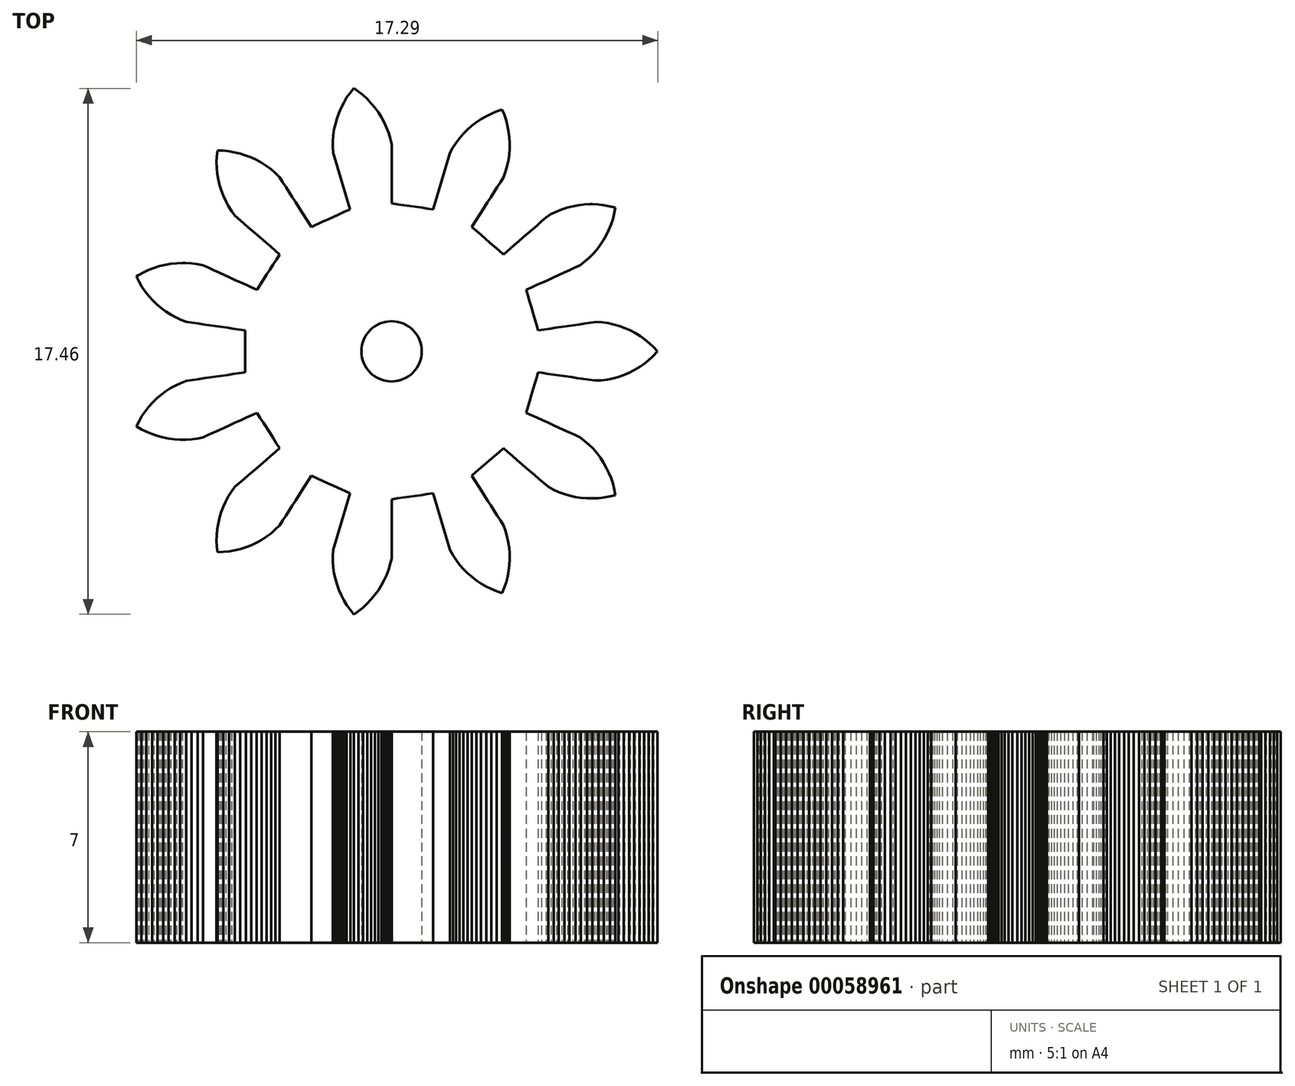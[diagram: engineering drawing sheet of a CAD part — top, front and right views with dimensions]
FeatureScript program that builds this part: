
annotation { "Feature Type Name" : "Feature", "Feature Type Description" : "" }
export const myFeature = defineFeature(function(context is Context, id is Id, definition is map)
    precondition{}
    {
        {
            var Q0;
            Q0=qCreatedBy(makeId("Top.planeOp"),FACE);
            var sketch = newSketch(context, id + "F0", { "sketchPlane" : qUnion([Q0])});
            skLineSegment(sketch, "E0", {"start": v(3.47, -0.7) * mm, "end": v(3.6, -0.72) * mm});
            skLineSegment(sketch, "E1", {"start": v(3.6, -0.72) * mm, "end": v(3.8, -0.75) * mm});
            skLineSegment(sketch, "E2", {"start": v(3.8, -0.75) * mm, "end": v(4, -0.77) * mm});
            skLineSegment(sketch, "E3", {"start": v(4, -0.77) * mm, "end": v(4.19, -0.8) * mm});
            skLineSegment(sketch, "E4", {"start": v(4.19, -0.8) * mm, "end": v(4.38, -0.83) * mm});
            skLineSegment(sketch, "E5", {"start": v(4.38, -0.83) * mm, "end": v(4.58, -0.86) * mm});
            skLineSegment(sketch, "E6", {"start": v(4.58, -0.86) * mm, "end": v(4.77, -0.89) * mm});
            skLineSegment(sketch, "E7", {"start": v(4.77, -0.89) * mm, "end": v(4.96, -0.91) * mm});
            skLineSegment(sketch, "E8", {"start": v(4.96, -0.91) * mm, "end": v(5.16, -0.94) * mm});
            skLineSegment(sketch, "E9", {"start": v(5.16, -0.94) * mm, "end": v(5.35, -0.97) * mm});
            skLineSegment(sketch, "E10", {"start": v(5.35, -0.97) * mm, "end": v(5.57, -0.97) * mm});
            skLineSegment(sketch, "E11", {"start": v(5.57, -0.97) * mm, "end": v(5.77, -0.94) * mm});
            skLineSegment(sketch, "E12", {"start": v(5.77, -0.94) * mm, "end": v(5.95, -0.9) * mm});
            skLineSegment(sketch, "E13", {"start": v(5.95, -0.9) * mm, "end": v(6.14, -0.85) * mm});
            skLineSegment(sketch, "E14", {"start": v(6.14, -0.85) * mm, "end": v(6.32, -0.79) * mm});
            skLineSegment(sketch, "E15", {"start": v(6.32, -0.79) * mm, "end": v(6.5, -0.7) * mm});
            skLineSegment(sketch, "E16", {"start": v(6.5, -0.7) * mm, "end": v(6.66, -0.62) * mm});
            skLineSegment(sketch, "E17", {"start": v(6.66, -0.62) * mm, "end": v(6.83, -0.52) * mm});
            skLineSegment(sketch, "E18", {"start": v(6.83, -0.52) * mm, "end": v(6.99, -0.42) * mm});
            skLineSegment(sketch, "E19", {"start": v(6.99, -0.42) * mm, "end": v(7.14, -0.3) * mm});
            skLineSegment(sketch, "E20", {"start": v(7.14, -0.3) * mm, "end": v(7.28, -0.17) * mm});
            skLineSegment(sketch, "E21", {"start": v(7.28, -0.17) * mm, "end": v(7.41, -0.02) * mm});
            skLineSegment(sketch, "E22", {"start": v(7.41, -0.02) * mm, "end": v(7.44, 0) * mm});
            skLineSegment(sketch, "E23", {"start": v(7.44, 0) * mm, "end": v(7.3, 0.14) * mm});
            skLineSegment(sketch, "E24", {"start": v(7.3, 0.14) * mm, "end": v(7.17, 0.27) * mm});
            skLineSegment(sketch, "E25", {"start": v(7.17, 0.27) * mm, "end": v(7.01, 0.4) * mm});
            skLineSegment(sketch, "E26", {"start": v(7.01, 0.4) * mm, "end": v(6.86, 0.5) * mm});
            skLineSegment(sketch, "E27", {"start": v(6.86, 0.5) * mm, "end": v(6.7, 0.6) * mm});
            skLineSegment(sketch, "E28", {"start": v(6.7, 0.6) * mm, "end": v(6.53, 0.7) * mm});
            skLineSegment(sketch, "E29", {"start": v(6.53, 0.7) * mm, "end": v(6.34, 0.77) * mm});
            skLineSegment(sketch, "E30", {"start": v(6.34, 0.77) * mm, "end": v(6.17, 0.84) * mm});
            skLineSegment(sketch, "E31", {"start": v(6.17, 0.84) * mm, "end": v(5.98, 0.9) * mm});
            skLineSegment(sketch, "E32", {"start": v(5.98, 0.9) * mm, "end": v(5.8, 0.93) * mm});
            skLineSegment(sketch, "E33", {"start": v(5.8, 0.93) * mm, "end": v(5.6, 0.96) * mm});
            skLineSegment(sketch, "E34", {"start": v(5.6, 0.96) * mm, "end": v(5.42, 0.98) * mm});
            skLineSegment(sketch, "E35", {"start": v(5.42, 0.98) * mm, "end": v(5.22, 0.95) * mm});
            skLineSegment(sketch, "E36", {"start": v(5.22, 0.95) * mm, "end": v(5.03, 0.92) * mm});
            skLineSegment(sketch, "E37", {"start": v(5.03, 0.92) * mm, "end": v(4.83, 0.9) * mm});
            skLineSegment(sketch, "E38", {"start": v(4.83, 0.9) * mm, "end": v(4.64, 0.87) * mm});
            skLineSegment(sketch, "E39", {"start": v(4.64, 0.87) * mm, "end": v(4.45, 0.84) * mm});
            skLineSegment(sketch, "E40", {"start": v(4.45, 0.84) * mm, "end": v(4.25, 0.81) * mm});
            skLineSegment(sketch, "E41", {"start": v(4.25, 0.81) * mm, "end": v(4.06, 0.78) * mm});
            skLineSegment(sketch, "E42", {"start": v(4.06, 0.78) * mm, "end": v(3.86, 0.75) * mm});
            skLineSegment(sketch, "E43", {"start": v(3.86, 0.75) * mm, "end": v(3.67, 0.73) * mm});
            skLineSegment(sketch, "E44", {"start": v(3.67, 0.73) * mm, "end": v(3.47, 0.7) * mm});
            skLineSegment(sketch, "E45", {"start": v(3.47, 0.7) * mm, "end": v(3.42, 0.89) * mm});
            skLineSegment(sketch, "E46", {"start": v(3.42, 0.89) * mm, "end": v(3.36, 1.08) * mm});
            skLineSegment(sketch, "E47", {"start": v(3.36, 1.08) * mm, "end": v(3.3, 1.27) * mm});
            skLineSegment(sketch, "E48", {"start": v(3.3, 1.27) * mm, "end": v(3.25, 1.46) * mm});
            skLineSegment(sketch, "E49", {"start": v(3.25, 1.46) * mm, "end": v(3.2, 1.65) * mm});
            skLineSegment(sketch, "E50", {"start": v(3.2, 1.65) * mm, "end": v(3.14, 1.84) * mm});
            skLineSegment(sketch, "E51", {"start": v(3.14, 1.84) * mm, "end": v(3.08, 2.04) * mm});
            skLineSegment(sketch, "E52", {"start": v(3.08, 2.04) * mm, "end": v(3.26, 2.12) * mm});
            skLineSegment(sketch, "E53", {"start": v(3.26, 2.12) * mm, "end": v(3.44, 2.2) * mm});
            skLineSegment(sketch, "E54", {"start": v(3.44, 2.2) * mm, "end": v(3.62, 2.29) * mm});
            skLineSegment(sketch, "E55", {"start": v(3.62, 2.29) * mm, "end": v(3.8, 2.37) * mm});
            skLineSegment(sketch, "E56", {"start": v(3.8, 2.37) * mm, "end": v(3.97, 2.45) * mm});
            skLineSegment(sketch, "E57", {"start": v(3.97, 2.45) * mm, "end": v(4.15, 2.53) * mm});
            skLineSegment(sketch, "E58", {"start": v(4.15, 2.53) * mm, "end": v(4.33, 2.61) * mm});
            skLineSegment(sketch, "E59", {"start": v(4.33, 2.61) * mm, "end": v(4.5, 2.7) * mm});
            skLineSegment(sketch, "E60", {"start": v(4.5, 2.7) * mm, "end": v(4.69, 2.77) * mm});
            skLineSegment(sketch, "E61", {"start": v(4.69, 2.77) * mm, "end": v(4.87, 2.86) * mm});
            skLineSegment(sketch, "E62", {"start": v(4.87, 2.86) * mm, "end": v(5.02, 2.98) * mm});
            skLineSegment(sketch, "E63", {"start": v(5.02, 2.98) * mm, "end": v(5.16, 3.1) * mm});
            skLineSegment(sketch, "E64", {"start": v(5.16, 3.1) * mm, "end": v(5.3, 3.24) * mm});
            skLineSegment(sketch, "E65", {"start": v(5.3, 3.24) * mm, "end": v(5.42, 3.38) * mm});
            skLineSegment(sketch, "E66", {"start": v(5.42, 3.38) * mm, "end": v(5.54, 3.54) * mm});
            skLineSegment(sketch, "E67", {"start": v(5.54, 3.54) * mm, "end": v(5.65, 3.7) * mm});
            skLineSegment(sketch, "E68", {"start": v(5.65, 3.7) * mm, "end": v(5.74, 3.87) * mm});
            skLineSegment(sketch, "E69", {"start": v(5.74, 3.87) * mm, "end": v(5.82, 4.03) * mm});
            skLineSegment(sketch, "E70", {"start": v(5.82, 4.03) * mm, "end": v(5.9, 4.22) * mm});
            skLineSegment(sketch, "E71", {"start": v(5.9, 4.22) * mm, "end": v(5.95, 4.4) * mm});
            skLineSegment(sketch, "E72", {"start": v(5.95, 4.4) * mm, "end": v(6, 4.59) * mm});
            skLineSegment(sketch, "E73", {"start": v(6, 4.59) * mm, "end": v(6.04, 4.77) * mm});
            skLineSegment(sketch, "E74", {"start": v(6.04, 4.77) * mm, "end": v(5.84, 4.82) * mm});
            skLineSegment(sketch, "E75", {"start": v(5.84, 4.82) * mm, "end": v(5.66, 4.85) * mm});
            skLineSegment(sketch, "E76", {"start": v(5.66, 4.85) * mm, "end": v(5.46, 4.87) * mm});
            skLineSegment(sketch, "E77", {"start": v(5.46, 4.87) * mm, "end": v(5.28, 4.88) * mm});
            skLineSegment(sketch, "E78", {"start": v(5.28, 4.88) * mm, "end": v(5.2, 4.88) * mm});
            skLineSegment(sketch, "E79", {"start": v(5.2, 4.88) * mm, "end": v(5, 4.87) * mm});
            skLineSegment(sketch, "E80", {"start": v(5, 4.87) * mm, "end": v(4.82, 4.85) * mm});
            skLineSegment(sketch, "E81", {"start": v(4.82, 4.85) * mm, "end": v(4.62, 4.82) * mm});
            skLineSegment(sketch, "E82", {"start": v(4.62, 4.82) * mm, "end": v(4.44, 4.77) * mm});
            skLineSegment(sketch, "E83", {"start": v(4.44, 4.77) * mm, "end": v(4.26, 4.7) * mm});
            skLineSegment(sketch, "E84", {"start": v(4.26, 4.7) * mm, "end": v(4.08, 4.64) * mm});
            skLineSegment(sketch, "E85", {"start": v(4.08, 4.64) * mm, "end": v(3.9, 4.55) * mm});
            skLineSegment(sketch, "E86", {"start": v(3.9, 4.55) * mm, "end": v(3.74, 4.44) * mm});
            skLineSegment(sketch, "E87", {"start": v(3.74, 4.44) * mm, "end": v(3.59, 4.31) * mm});
            skLineSegment(sketch, "E88", {"start": v(3.59, 4.31) * mm, "end": v(3.44, 4.18) * mm});
            skLineSegment(sketch, "E89", {"start": v(3.44, 4.18) * mm, "end": v(3.29, 4.05) * mm});
            skLineSegment(sketch, "E90", {"start": v(3.29, 4.05) * mm, "end": v(3.14, 3.92) * mm});
            skLineSegment(sketch, "E91", {"start": v(3.14, 3.92) * mm, "end": v(2.99, 3.8) * mm});
            skLineSegment(sketch, "E92", {"start": v(2.99, 3.8) * mm, "end": v(2.84, 3.66) * mm});
            skLineSegment(sketch, "E93", {"start": v(2.84, 3.66) * mm, "end": v(2.69, 3.53) * mm});
            skLineSegment(sketch, "E94", {"start": v(2.69, 3.53) * mm, "end": v(2.54, 3.4) * mm});
            skLineSegment(sketch, "E95", {"start": v(2.54, 3.4) * mm, "end": v(2.37, 3.26) * mm});
            skLineSegment(sketch, "E96", {"start": v(2.37, 3.26) * mm, "end": v(2.32, 3.22) * mm});
            skLineSegment(sketch, "E97", {"start": v(2.32, 3.22) * mm, "end": v(2.17, 3.35) * mm});
            skLineSegment(sketch, "E98", {"start": v(2.17, 3.35) * mm, "end": v(2.02, 3.48) * mm});
            skLineSegment(sketch, "E99", {"start": v(2.02, 3.48) * mm, "end": v(1.87, 3.6) * mm});
            skLineSegment(sketch, "E100", {"start": v(1.87, 3.6) * mm, "end": v(1.72, 3.74) * mm});
            skLineSegment(sketch, "E101", {"start": v(1.72, 3.74) * mm, "end": v(1.57, 3.87) * mm});
            skLineSegment(sketch, "E102", {"start": v(1.57, 3.87) * mm, "end": v(1.42, 4) * mm});
            skLineSegment(sketch, "E103", {"start": v(1.42, 4) * mm, "end": v(1.27, 4.13) * mm});
            skLineSegment(sketch, "E104", {"start": v(1.27, 4.13) * mm, "end": v(1.37, 4.3) * mm});
            skLineSegment(sketch, "E105", {"start": v(1.37, 4.3) * mm, "end": v(1.48, 4.46) * mm});
            skLineSegment(sketch, "E106", {"start": v(1.48, 4.46) * mm, "end": v(1.59, 4.63) * mm});
            skLineSegment(sketch, "E107", {"start": v(1.59, 4.63) * mm, "end": v(1.7, 4.8) * mm});
            skLineSegment(sketch, "E108", {"start": v(1.7, 4.8) * mm, "end": v(1.8, 4.96) * mm});
            skLineSegment(sketch, "E109", {"start": v(1.8, 4.96) * mm, "end": v(1.9, 5.12) * mm});
            skLineSegment(sketch, "E110", {"start": v(1.9, 5.12) * mm, "end": v(2.01, 5.29) * mm});
            skLineSegment(sketch, "E111", {"start": v(2.01, 5.29) * mm, "end": v(2.12, 5.45) * mm});
            skLineSegment(sketch, "E112", {"start": v(2.12, 5.45) * mm, "end": v(2.22, 5.62) * mm});
            skLineSegment(sketch, "E113", {"start": v(2.22, 5.62) * mm, "end": v(2.33, 5.78) * mm});
            skLineSegment(sketch, "E114", {"start": v(2.33, 5.78) * mm, "end": v(2.4, 5.97) * mm});
            skLineSegment(sketch, "E115", {"start": v(2.4, 5.97) * mm, "end": v(2.45, 6.15) * mm});
            skLineSegment(sketch, "E116", {"start": v(2.45, 6.15) * mm, "end": v(2.49, 6.34) * mm});
            skLineSegment(sketch, "E117", {"start": v(2.49, 6.34) * mm, "end": v(2.52, 6.53) * mm});
            skLineSegment(sketch, "E118", {"start": v(2.52, 6.53) * mm, "end": v(2.53, 6.72) * mm});
            skLineSegment(sketch, "E119", {"start": v(2.53, 6.72) * mm, "end": v(2.53, 6.91) * mm});
            skLineSegment(sketch, "E120", {"start": v(2.53, 6.91) * mm, "end": v(2.52, 7.1) * mm});
            skLineSegment(sketch, "E121", {"start": v(2.52, 7.1) * mm, "end": v(2.5, 7.3) * mm});
            skLineSegment(sketch, "E122", {"start": v(2.5, 7.3) * mm, "end": v(2.46, 7.49) * mm});
            skLineSegment(sketch, "E123", {"start": v(2.46, 7.49) * mm, "end": v(2.41, 7.67) * mm});
            skLineSegment(sketch, "E124", {"start": v(2.41, 7.67) * mm, "end": v(2.35, 7.85) * mm});
            skLineSegment(sketch, "E125", {"start": v(2.35, 7.85) * mm, "end": v(2.28, 8.03) * mm});
            skLineSegment(sketch, "E126", {"start": v(2.28, 8.03) * mm, "end": v(2.1, 7.96) * mm});
            skLineSegment(sketch, "E127", {"start": v(2.1, 7.96) * mm, "end": v(1.92, 7.9) * mm});
            skLineSegment(sketch, "E128", {"start": v(1.92, 7.9) * mm, "end": v(1.74, 7.8) * mm});
            skLineSegment(sketch, "E129", {"start": v(1.74, 7.8) * mm, "end": v(1.58, 7.71) * mm});
            skLineSegment(sketch, "E130", {"start": v(1.58, 7.71) * mm, "end": v(1.42, 7.6) * mm});
            skLineSegment(sketch, "E131", {"start": v(1.42, 7.6) * mm, "end": v(1.27, 7.49) * mm});
            skLineSegment(sketch, "E132", {"start": v(1.27, 7.49) * mm, "end": v(1.12, 7.35) * mm});
            skLineSegment(sketch, "E133", {"start": v(1.12, 7.35) * mm, "end": v(1, 7.22) * mm});
            skLineSegment(sketch, "E134", {"start": v(1, 7.22) * mm, "end": v(0.86, 7.07) * mm});
            skLineSegment(sketch, "E135", {"start": v(0.86, 7.07) * mm, "end": v(0.75, 6.92) * mm});
            skLineSegment(sketch, "E136", {"start": v(0.75, 6.92) * mm, "end": v(0.64, 6.76) * mm});
            skLineSegment(sketch, "E137", {"start": v(0.64, 6.76) * mm, "end": v(0.55, 6.6) * mm});
            skLineSegment(sketch, "E138", {"start": v(0.55, 6.6) * mm, "end": v(0.5, 6.4) * mm});
            skLineSegment(sketch, "E139", {"start": v(0.5, 6.4) * mm, "end": v(0.44, 6.22) * mm});
            skLineSegment(sketch, "E140", {"start": v(0.44, 6.22) * mm, "end": v(0.38, 6.03) * mm});
            skLineSegment(sketch, "E141", {"start": v(0.38, 6.03) * mm, "end": v(0.33, 5.84) * mm});
            skLineSegment(sketch, "E142", {"start": v(0.33, 5.84) * mm, "end": v(0.27, 5.65) * mm});
            skLineSegment(sketch, "E143", {"start": v(0.27, 5.65) * mm, "end": v(0.22, 5.47) * mm});
            skLineSegment(sketch, "E144", {"start": v(0.22, 5.47) * mm, "end": v(0.16, 5.28) * mm});
            skLineSegment(sketch, "E145", {"start": v(0.16, 5.28) * mm, "end": v(0.1, 5.09) * mm});
            skLineSegment(sketch, "E146", {"start": v(0.1, 5.09) * mm, "end": v(0.05, 4.9) * mm});
            skLineSegment(sketch, "E147", {"start": v(0.05, 4.9) * mm, "end": v(0, 4.71) * mm});
            skLineSegment(sketch, "E148", {"start": v(0, 4.71) * mm, "end": v(-0.2, 4.74) * mm});
            skLineSegment(sketch, "E149", {"start": v(-0.2, 4.74) * mm, "end": v(-0.4, 4.77) * mm});
            skLineSegment(sketch, "E150", {"start": v(-0.4, 4.77) * mm, "end": v(-0.6, 4.8) * mm});
            skLineSegment(sketch, "E151", {"start": v(-0.6, 4.8) * mm, "end": v(-0.79, 4.83) * mm});
            skLineSegment(sketch, "E152", {"start": v(-0.79, 4.83) * mm, "end": v(-0.99, 4.85) * mm});
            skLineSegment(sketch, "E153", {"start": v(-0.99, 4.85) * mm, "end": v(-1.18, 4.88) * mm});
            skLineSegment(sketch, "E154", {"start": v(-1.18, 4.88) * mm, "end": v(-1.39, 4.91) * mm});
            skLineSegment(sketch, "E155", {"start": v(-1.39, 4.91) * mm, "end": v(-1.39, 5.1) * mm});
            skLineSegment(sketch, "E156", {"start": v(-1.39, 5.1) * mm, "end": v(-1.39, 5.3) * mm});
            skLineSegment(sketch, "E157", {"start": v(-1.39, 5.3) * mm, "end": v(-1.39, 5.5) * mm});
            skLineSegment(sketch, "E158", {"start": v(-1.39, 5.5) * mm, "end": v(-1.39, 5.7) * mm});
            skLineSegment(sketch, "E159", {"start": v(-1.39, 5.7) * mm, "end": v(-1.39, 5.9) * mm});
            skLineSegment(sketch, "E160", {"start": v(-1.39, 5.9) * mm, "end": v(-1.39, 6.09) * mm});
            skLineSegment(sketch, "E161", {"start": v(-1.39, 6.09) * mm, "end": v(-1.39, 6.29) * mm});
            skLineSegment(sketch, "E162", {"start": v(-1.39, 6.29) * mm, "end": v(-1.39, 6.48) * mm});
            skLineSegment(sketch, "E163", {"start": v(-1.39, 6.48) * mm, "end": v(-1.39, 6.68) * mm});
            skLineSegment(sketch, "E164", {"start": v(-1.39, 6.68) * mm, "end": v(-1.39, 6.88) * mm});
            skLineSegment(sketch, "E165", {"start": v(-1.39, 6.88) * mm, "end": v(-1.43, 7.07) * mm});
            skLineSegment(sketch, "E166", {"start": v(-1.43, 7.07) * mm, "end": v(-1.49, 7.25) * mm});
            skLineSegment(sketch, "E167", {"start": v(-1.49, 7.25) * mm, "end": v(-1.56, 7.43) * mm});
            skLineSegment(sketch, "E168", {"start": v(-1.56, 7.43) * mm, "end": v(-1.63, 7.6) * mm});
            skLineSegment(sketch, "E169", {"start": v(-1.63, 7.6) * mm, "end": v(-1.73, 7.77) * mm});
            skLineSegment(sketch, "E170", {"start": v(-1.73, 7.77) * mm, "end": v(-1.83, 7.93) * mm});
            skLineSegment(sketch, "E171", {"start": v(-1.83, 7.93) * mm, "end": v(-1.94, 8.1) * mm});
            skLineSegment(sketch, "E172", {"start": v(-1.94, 8.1) * mm, "end": v(-2.06, 8.24) * mm});
            skLineSegment(sketch, "E173", {"start": v(-2.06, 8.24) * mm, "end": v(-2.2, 8.38) * mm});
            skLineSegment(sketch, "E174", {"start": v(-2.2, 8.38) * mm, "end": v(-2.34, 8.5) * mm});
            skLineSegment(sketch, "E175", {"start": v(-2.34, 8.5) * mm, "end": v(-2.5, 8.63) * mm});
            skLineSegment(sketch, "E176", {"start": v(-2.5, 8.63) * mm, "end": v(-2.64, 8.73) * mm});
            skLineSegment(sketch, "E177", {"start": v(-2.64, 8.73) * mm, "end": v(-2.77, 8.58) * mm});
            skLineSegment(sketch, "E178", {"start": v(-2.77, 8.58) * mm, "end": v(-2.87, 8.43) * mm});
            skLineSegment(sketch, "E179", {"start": v(-2.87, 8.43) * mm, "end": v(-2.97, 8.26) * mm});
            skLineSegment(sketch, "E180", {"start": v(-2.97, 8.26) * mm, "end": v(-3.06, 8.1) * mm});
            skLineSegment(sketch, "E181", {"start": v(-3.06, 8.1) * mm, "end": v(-3.14, 7.9) * mm});
            skLineSegment(sketch, "E182", {"start": v(-3.14, 7.9) * mm, "end": v(-3.2, 7.73) * mm});
            skLineSegment(sketch, "E183", {"start": v(-3.2, 7.73) * mm, "end": v(-3.25, 7.54) * mm});
            skLineSegment(sketch, "E184", {"start": v(-3.25, 7.54) * mm, "end": v(-3.3, 7.36) * mm});
            skLineSegment(sketch, "E185", {"start": v(-3.3, 7.36) * mm, "end": v(-3.32, 7.16) * mm});
            skLineSegment(sketch, "E186", {"start": v(-3.32, 7.16) * mm, "end": v(-3.33, 6.98) * mm});
            skLineSegment(sketch, "E187", {"start": v(-3.33, 6.98) * mm, "end": v(-3.33, 6.78) * mm});
            skLineSegment(sketch, "E188", {"start": v(-3.33, 6.78) * mm, "end": v(-3.32, 6.6) * mm});
            skLineSegment(sketch, "E189", {"start": v(-3.32, 6.6) * mm, "end": v(-3.27, 6.4) * mm});
            skLineSegment(sketch, "E190", {"start": v(-3.27, 6.4) * mm, "end": v(-3.21, 6.22) * mm});
            skLineSegment(sketch, "E191", {"start": v(-3.21, 6.22) * mm, "end": v(-3.16, 6.03) * mm});
            skLineSegment(sketch, "E192", {"start": v(-3.16, 6.03) * mm, "end": v(-3.1, 5.84) * mm});
            skLineSegment(sketch, "E193", {"start": v(-3.1, 5.84) * mm, "end": v(-3.05, 5.65) * mm});
            skLineSegment(sketch, "E194", {"start": v(-3.05, 5.65) * mm, "end": v(-3, 5.47) * mm});
            skLineSegment(sketch, "E195", {"start": v(-3, 5.47) * mm, "end": v(-2.94, 5.28) * mm});
            skLineSegment(sketch, "E196", {"start": v(-2.94, 5.28) * mm, "end": v(-2.88, 5.09) * mm});
            skLineSegment(sketch, "E197", {"start": v(-2.88, 5.09) * mm, "end": v(-2.83, 4.9) * mm});
            skLineSegment(sketch, "E198", {"start": v(-2.83, 4.9) * mm, "end": v(-2.77, 4.71) * mm});
            skLineSegment(sketch, "E199", {"start": v(-2.77, 4.71) * mm, "end": v(-2.95, 4.63) * mm});
            skLineSegment(sketch, "E200", {"start": v(-2.95, 4.63) * mm, "end": v(-3.13, 4.55) * mm});
            skLineSegment(sketch, "E201", {"start": v(-3.13, 4.55) * mm, "end": v(-3.31, 4.46) * mm});
            skLineSegment(sketch, "E202", {"start": v(-3.31, 4.46) * mm, "end": v(-3.5, 4.38) * mm});
            skLineSegment(sketch, "E203", {"start": v(-3.5, 4.38) * mm, "end": v(-3.67, 4.3) * mm});
            skLineSegment(sketch, "E204", {"start": v(-3.67, 4.3) * mm, "end": v(-3.86, 4.22) * mm});
            skLineSegment(sketch, "E205", {"start": v(-3.86, 4.22) * mm, "end": v(-4.04, 4.13) * mm});
            skLineSegment(sketch, "E206", {"start": v(-4.04, 4.13) * mm, "end": v(-4.15, 4.3) * mm});
            skLineSegment(sketch, "E207", {"start": v(-4.15, 4.3) * mm, "end": v(-4.25, 4.46) * mm});
            skLineSegment(sketch, "E208", {"start": v(-4.25, 4.46) * mm, "end": v(-4.36, 4.63) * mm});
            skLineSegment(sketch, "E209", {"start": v(-4.36, 4.63) * mm, "end": v(-4.47, 4.8) * mm});
            skLineSegment(sketch, "E210", {"start": v(-4.47, 4.8) * mm, "end": v(-4.57, 4.96) * mm});
            skLineSegment(sketch, "E211", {"start": v(-4.57, 4.96) * mm, "end": v(-4.68, 5.12) * mm});
            skLineSegment(sketch, "E212", {"start": v(-4.68, 5.12) * mm, "end": v(-4.79, 5.29) * mm});
            skLineSegment(sketch, "E213", {"start": v(-4.79, 5.29) * mm, "end": v(-4.9, 5.45) * mm});
            skLineSegment(sketch, "E214", {"start": v(-4.9, 5.45) * mm, "end": v(-5, 5.62) * mm});
            skLineSegment(sketch, "E215", {"start": v(-5, 5.62) * mm, "end": v(-5.1, 5.78) * mm});
            skLineSegment(sketch, "E216", {"start": v(-5.1, 5.78) * mm, "end": v(-5.25, 5.92) * mm});
            skLineSegment(sketch, "E217", {"start": v(-5.25, 5.92) * mm, "end": v(-5.39, 6.04) * mm});
            skLineSegment(sketch, "E218", {"start": v(-5.39, 6.04) * mm, "end": v(-5.55, 6.16) * mm});
            skLineSegment(sketch, "E219", {"start": v(-5.55, 6.16) * mm, "end": v(-5.7, 6.26) * mm});
            skLineSegment(sketch, "E220", {"start": v(-5.7, 6.26) * mm, "end": v(-5.88, 6.36) * mm});
            skLineSegment(sketch, "E221", {"start": v(-5.88, 6.36) * mm, "end": v(-6.04, 6.44) * mm});
            skLineSegment(sketch, "E222", {"start": v(-6.04, 6.44) * mm, "end": v(-6.23, 6.5) * mm});
            skLineSegment(sketch, "E223", {"start": v(-6.23, 6.5) * mm, "end": v(-6.4, 6.56) * mm});
            skLineSegment(sketch, "E224", {"start": v(-6.4, 6.56) * mm, "end": v(-6.6, 6.6) * mm});
            skLineSegment(sketch, "E225", {"start": v(-6.6, 6.6) * mm, "end": v(-6.78, 6.64) * mm});
            skLineSegment(sketch, "E226", {"start": v(-6.78, 6.64) * mm, "end": v(-6.98, 6.66) * mm});
            skLineSegment(sketch, "E227", {"start": v(-6.98, 6.66) * mm, "end": v(-7.17, 6.67) * mm});
            skLineSegment(sketch, "E228", {"start": v(-7.17, 6.67) * mm, "end": v(-7.18, 6.47) * mm});
            skLineSegment(sketch, "E229", {"start": v(-7.18, 6.47) * mm, "end": v(-7.2, 6.29) * mm});
            skLineSegment(sketch, "E230", {"start": v(-7.2, 6.29) * mm, "end": v(-7.19, 6.09) * mm});
            skLineSegment(sketch, "E231", {"start": v(-7.19, 6.09) * mm, "end": v(-7.17, 5.9) * mm});
            skLineSegment(sketch, "E232", {"start": v(-7.17, 5.9) * mm, "end": v(-7.14, 5.7) * mm});
            skLineSegment(sketch, "E233", {"start": v(-7.14, 5.7) * mm, "end": v(-7.1, 5.53) * mm});
            skLineSegment(sketch, "E234", {"start": v(-7.1, 5.53) * mm, "end": v(-7.04, 5.34) * mm});
            skLineSegment(sketch, "E235", {"start": v(-7.04, 5.34) * mm, "end": v(-6.97, 5.16) * mm});
            skLineSegment(sketch, "E236", {"start": v(-6.97, 5.16) * mm, "end": v(-6.89, 4.98) * mm});
            skLineSegment(sketch, "E237", {"start": v(-6.89, 4.98) * mm, "end": v(-6.8, 4.82) * mm});
            skLineSegment(sketch, "E238", {"start": v(-6.8, 4.82) * mm, "end": v(-6.7, 4.65) * mm});
            skLineSegment(sketch, "E239", {"start": v(-6.7, 4.65) * mm, "end": v(-6.58, 4.5) * mm});
            skLineSegment(sketch, "E240", {"start": v(-6.58, 4.5) * mm, "end": v(-6.43, 4.37) * mm});
            skLineSegment(sketch, "E241", {"start": v(-6.43, 4.37) * mm, "end": v(-6.29, 4.25) * mm});
            skLineSegment(sketch, "E242", {"start": v(-6.29, 4.25) * mm, "end": v(-6.14, 4.12) * mm});
            skLineSegment(sketch, "E243", {"start": v(-6.14, 4.12) * mm, "end": v(-5.99, 3.99) * mm});
            skLineSegment(sketch, "E244", {"start": v(-5.99, 3.99) * mm, "end": v(-5.84, 3.86) * mm});
            skLineSegment(sketch, "E245", {"start": v(-5.84, 3.86) * mm, "end": v(-5.7, 3.73) * mm});
            skLineSegment(sketch, "E246", {"start": v(-5.7, 3.73) * mm, "end": v(-5.54, 3.6) * mm});
            skLineSegment(sketch, "E247", {"start": v(-5.54, 3.6) * mm, "end": v(-5.4, 3.47) * mm});
            skLineSegment(sketch, "E248", {"start": v(-5.4, 3.47) * mm, "end": v(-5.25, 3.34) * mm});
            skLineSegment(sketch, "E249", {"start": v(-5.25, 3.34) * mm, "end": v(-5.1, 3.22) * mm});
            skLineSegment(sketch, "E250", {"start": v(-5.1, 3.22) * mm, "end": v(-5.2, 3.05) * mm});
            skLineSegment(sketch, "E251", {"start": v(-5.2, 3.05) * mm, "end": v(-5.31, 2.88) * mm});
            skLineSegment(sketch, "E252", {"start": v(-5.31, 2.88) * mm, "end": v(-5.42, 2.71) * mm});
            skLineSegment(sketch, "E253", {"start": v(-5.42, 2.71) * mm, "end": v(-5.53, 2.55) * mm});
            skLineSegment(sketch, "E254", {"start": v(-5.53, 2.55) * mm, "end": v(-5.64, 2.38) * mm});
            skLineSegment(sketch, "E255", {"start": v(-5.64, 2.38) * mm, "end": v(-5.74, 2.21) * mm});
            skLineSegment(sketch, "E256", {"start": v(-5.74, 2.21) * mm, "end": v(-5.85, 2.04) * mm});
            skLineSegment(sketch, "E257", {"start": v(-5.85, 2.04) * mm, "end": v(-6.03, 2.12) * mm});
            skLineSegment(sketch, "E258", {"start": v(-6.03, 2.12) * mm, "end": v(-6.21, 2.2) * mm});
            skLineSegment(sketch, "E259", {"start": v(-6.21, 2.2) * mm, "end": v(-6.4, 2.29) * mm});
            skLineSegment(sketch, "E260", {"start": v(-6.4, 2.29) * mm, "end": v(-6.57, 2.37) * mm});
            skLineSegment(sketch, "E261", {"start": v(-6.57, 2.37) * mm, "end": v(-6.75, 2.45) * mm});
            skLineSegment(sketch, "E262", {"start": v(-6.75, 2.45) * mm, "end": v(-6.93, 2.53) * mm});
            skLineSegment(sketch, "E263", {"start": v(-6.93, 2.53) * mm, "end": v(-7.1, 2.61) * mm});
            skLineSegment(sketch, "E264", {"start": v(-7.1, 2.61) * mm, "end": v(-7.28, 2.7) * mm});
            skLineSegment(sketch, "E265", {"start": v(-7.28, 2.7) * mm, "end": v(-7.46, 2.77) * mm});
            skLineSegment(sketch, "E266", {"start": v(-7.46, 2.77) * mm, "end": v(-7.64, 2.86) * mm});
            skLineSegment(sketch, "E267", {"start": v(-7.64, 2.86) * mm, "end": v(-7.84, 2.9) * mm});
            skLineSegment(sketch, "E268", {"start": v(-7.84, 2.9) * mm, "end": v(-8.02, 2.92) * mm});
            skLineSegment(sketch, "E269", {"start": v(-8.02, 2.92) * mm, "end": v(-8.22, 2.93) * mm});
            skLineSegment(sketch, "E270", {"start": v(-8.22, 2.93) * mm, "end": v(-8.33, 2.94) * mm});
            skLineSegment(sketch, "E271", {"start": v(-8.33, 2.94) * mm, "end": v(-8.52, 2.93) * mm});
            skLineSegment(sketch, "E272", {"start": v(-8.52, 2.93) * mm, "end": v(-8.7, 2.9) * mm});
            skLineSegment(sketch, "E273", {"start": v(-8.7, 2.9) * mm, "end": v(-8.9, 2.87) * mm});
            skLineSegment(sketch, "E274", {"start": v(-8.9, 2.87) * mm, "end": v(-9.08, 2.83) * mm});
            skLineSegment(sketch, "E275", {"start": v(-9.08, 2.83) * mm, "end": v(-9.27, 2.77) * mm});
            skLineSegment(sketch, "E276", {"start": v(-9.27, 2.77) * mm, "end": v(-9.45, 2.7) * mm});
            skLineSegment(sketch, "E277", {"start": v(-9.45, 2.7) * mm, "end": v(-9.63, 2.62) * mm});
            skLineSegment(sketch, "E278", {"start": v(-9.63, 2.62) * mm, "end": v(-9.79, 2.53) * mm});
            skLineSegment(sketch, "E279", {"start": v(-9.79, 2.53) * mm, "end": v(-9.85, 2.49) * mm});
            skLineSegment(sketch, "E280", {"start": v(-9.85, 2.49) * mm, "end": v(-9.76, 2.3) * mm});
            skLineSegment(sketch, "E281", {"start": v(-9.76, 2.3) * mm, "end": v(-9.67, 2.15) * mm});
            skLineSegment(sketch, "E282", {"start": v(-9.67, 2.15) * mm, "end": v(-9.56, 1.99) * mm});
            skLineSegment(sketch, "E283", {"start": v(-9.56, 1.99) * mm, "end": v(-9.44, 1.84) * mm});
            skLineSegment(sketch, "E284", {"start": v(-9.44, 1.84) * mm, "end": v(-9.3, 1.7) * mm});
            skLineSegment(sketch, "E285", {"start": v(-9.3, 1.7) * mm, "end": v(-9.18, 1.56) * mm});
            skLineSegment(sketch, "E286", {"start": v(-9.18, 1.56) * mm, "end": v(-9.02, 1.44) * mm});
            skLineSegment(sketch, "E287", {"start": v(-9.02, 1.44) * mm, "end": v(-8.88, 1.32) * mm});
            skLineSegment(sketch, "E288", {"start": v(-8.88, 1.32) * mm, "end": v(-8.7, 1.22) * mm});
            skLineSegment(sketch, "E289", {"start": v(-8.7, 1.22) * mm, "end": v(-8.55, 1.13) * mm});
            skLineSegment(sketch, "E290", {"start": v(-8.55, 1.13) * mm, "end": v(-8.36, 1.05) * mm});
            skLineSegment(sketch, "E291", {"start": v(-8.36, 1.05) * mm, "end": v(-8.2, 0.98) * mm});
            skLineSegment(sketch, "E292", {"start": v(-8.2, 0.98) * mm, "end": v(-8, 0.95) * mm});
            skLineSegment(sketch, "E293", {"start": v(-8, 0.95) * mm, "end": v(-7.8, 0.92) * mm});
            skLineSegment(sketch, "E294", {"start": v(-7.8, 0.92) * mm, "end": v(-7.6, 0.9) * mm});
            skLineSegment(sketch, "E295", {"start": v(-7.6, 0.9) * mm, "end": v(-7.41, 0.87) * mm});
            skLineSegment(sketch, "E296", {"start": v(-7.41, 0.87) * mm, "end": v(-7.22, 0.84) * mm});
            skLineSegment(sketch, "E297", {"start": v(-7.22, 0.84) * mm, "end": v(-7.03, 0.81) * mm});
            skLineSegment(sketch, "E298", {"start": v(-7.03, 0.81) * mm, "end": v(-6.83, 0.78) * mm});
            skLineSegment(sketch, "E299", {"start": v(-6.83, 0.78) * mm, "end": v(-6.64, 0.75) * mm});
            skLineSegment(sketch, "E300", {"start": v(-6.64, 0.75) * mm, "end": v(-6.44, 0.73) * mm});
            skLineSegment(sketch, "E301", {"start": v(-6.44, 0.73) * mm, "end": v(-6.25, 0.7) * mm});
            skLineSegment(sketch, "E302", {"start": v(-6.25, 0.7) * mm, "end": v(-6.25, 0.5) * mm});
            skLineSegment(sketch, "E303", {"start": v(-6.25, 0.5) * mm, "end": v(-6.25, 0.3) * mm});
            skLineSegment(sketch, "E304", {"start": v(-6.25, 0.3) * mm, "end": v(-6.25, 0.1) * mm});
            skLineSegment(sketch, "E305", {"start": v(-6.25, 0.1) * mm, "end": v(-6.25, -0.1) * mm});
            skLineSegment(sketch, "E306", {"start": v(-6.25, -0.1) * mm, "end": v(-6.25, -0.3) * mm});
            skLineSegment(sketch, "E307", {"start": v(-6.25, -0.3) * mm, "end": v(-6.25, -0.5) * mm});
            skLineSegment(sketch, "E308", {"start": v(-6.25, -0.5) * mm, "end": v(-6.25, -0.7) * mm});
            skLineSegment(sketch, "E309", {"start": v(-6.25, -0.7) * mm, "end": v(-6.44, -0.73) * mm});
            skLineSegment(sketch, "E310", {"start": v(-6.44, -0.73) * mm, "end": v(-6.64, -0.75) * mm});
            skLineSegment(sketch, "E311", {"start": v(-6.64, -0.75) * mm, "end": v(-6.83, -0.78) * mm});
            skLineSegment(sketch, "E312", {"start": v(-6.83, -0.78) * mm, "end": v(-7.03, -0.81) * mm});
            skLineSegment(sketch, "E313", {"start": v(-7.03, -0.81) * mm, "end": v(-7.22, -0.84) * mm});
            skLineSegment(sketch, "E314", {"start": v(-7.22, -0.84) * mm, "end": v(-7.41, -0.87) * mm});
            skLineSegment(sketch, "E315", {"start": v(-7.41, -0.87) * mm, "end": v(-7.6, -0.9) * mm});
            skLineSegment(sketch, "E316", {"start": v(-7.6, -0.9) * mm, "end": v(-7.8, -0.92) * mm});
            skLineSegment(sketch, "E317", {"start": v(-7.8, -0.92) * mm, "end": v(-8, -0.95) * mm});
            skLineSegment(sketch, "E318", {"start": v(-8, -0.95) * mm, "end": v(-8.2, -0.98) * mm});
            skLineSegment(sketch, "E319", {"start": v(-8.2, -0.98) * mm, "end": v(-8.38, -1.05) * mm});
            skLineSegment(sketch, "E320", {"start": v(-8.38, -1.05) * mm, "end": v(-8.55, -1.13) * mm});
            skLineSegment(sketch, "E321", {"start": v(-8.55, -1.13) * mm, "end": v(-8.72, -1.23) * mm});
            skLineSegment(sketch, "E322", {"start": v(-8.72, -1.23) * mm, "end": v(-8.88, -1.32) * mm});
            skLineSegment(sketch, "E323", {"start": v(-8.88, -1.32) * mm, "end": v(-9.03, -1.44) * mm});
            skLineSegment(sketch, "E324", {"start": v(-9.03, -1.44) * mm, "end": v(-9.18, -1.56) * mm});
            skLineSegment(sketch, "E325", {"start": v(-9.18, -1.56) * mm, "end": v(-9.32, -1.7) * mm});
            skLineSegment(sketch, "E326", {"start": v(-9.32, -1.7) * mm, "end": v(-9.44, -1.84) * mm});
            skLineSegment(sketch, "E327", {"start": v(-9.44, -1.84) * mm, "end": v(-9.56, -2) * mm});
            skLineSegment(sketch, "E328", {"start": v(-9.56, -2) * mm, "end": v(-9.67, -2.15) * mm});
            skLineSegment(sketch, "E329", {"start": v(-9.67, -2.15) * mm, "end": v(-9.77, -2.32) * mm});
            skLineSegment(sketch, "E330", {"start": v(-9.77, -2.32) * mm, "end": v(-9.85, -2.49) * mm});
            skLineSegment(sketch, "E331", {"start": v(-9.85, -2.49) * mm, "end": v(-9.68, -2.59) * mm});
            skLineSegment(sketch, "E332", {"start": v(-9.68, -2.59) * mm, "end": v(-9.52, -2.67) * mm});
            skLineSegment(sketch, "E333", {"start": v(-9.52, -2.67) * mm, "end": v(-9.33, -2.75) * mm});
            skLineSegment(sketch, "E334", {"start": v(-9.33, -2.75) * mm, "end": v(-9.16, -2.8) * mm});
            skLineSegment(sketch, "E335", {"start": v(-9.16, -2.8) * mm, "end": v(-8.97, -2.86) * mm});
            skLineSegment(sketch, "E336", {"start": v(-8.97, -2.86) * mm, "end": v(-8.78, -2.9) * mm});
            skLineSegment(sketch, "E337", {"start": v(-8.78, -2.9) * mm, "end": v(-8.59, -2.92) * mm});
            skLineSegment(sketch, "E338", {"start": v(-8.59, -2.92) * mm, "end": v(-8.4, -2.93) * mm});
            skLineSegment(sketch, "E339", {"start": v(-8.4, -2.93) * mm, "end": v(-8.2, -2.93) * mm});
            skLineSegment(sketch, "E340", {"start": v(-8.2, -2.93) * mm, "end": v(-8.02, -2.92) * mm});
            skLineSegment(sketch, "E341", {"start": v(-8.02, -2.92) * mm, "end": v(-7.82, -2.9) * mm});
            skLineSegment(sketch, "E342", {"start": v(-7.82, -2.9) * mm, "end": v(-7.64, -2.86) * mm});
            skLineSegment(sketch, "E343", {"start": v(-7.64, -2.86) * mm, "end": v(-7.46, -2.77) * mm});
            skLineSegment(sketch, "E344", {"start": v(-7.46, -2.77) * mm, "end": v(-7.28, -2.7) * mm});
            skLineSegment(sketch, "E345", {"start": v(-7.28, -2.7) * mm, "end": v(-7.1, -2.61) * mm});
            skLineSegment(sketch, "E346", {"start": v(-7.1, -2.61) * mm, "end": v(-6.93, -2.53) * mm});
            skLineSegment(sketch, "E347", {"start": v(-6.93, -2.53) * mm, "end": v(-6.75, -2.45) * mm});
            skLineSegment(sketch, "E348", {"start": v(-6.75, -2.45) * mm, "end": v(-6.57, -2.37) * mm});
            skLineSegment(sketch, "E349", {"start": v(-6.57, -2.37) * mm, "end": v(-6.4, -2.29) * mm});
            skLineSegment(sketch, "E350", {"start": v(-6.4, -2.29) * mm, "end": v(-6.21, -2.2) * mm});
            skLineSegment(sketch, "E351", {"start": v(-6.21, -2.2) * mm, "end": v(-6.03, -2.12) * mm});
            skLineSegment(sketch, "E352", {"start": v(-6.03, -2.12) * mm, "end": v(-5.85, -2.04) * mm});
            skLineSegment(sketch, "E353", {"start": v(-5.85, -2.04) * mm, "end": v(-5.75, -2.2) * mm});
            skLineSegment(sketch, "E354", {"start": v(-5.75, -2.2) * mm, "end": v(-5.64, -2.37) * mm});
            skLineSegment(sketch, "E355", {"start": v(-5.64, -2.37) * mm, "end": v(-5.53, -2.54) * mm});
            skLineSegment(sketch, "E356", {"start": v(-5.53, -2.54) * mm, "end": v(-5.43, -2.7) * mm});
            skLineSegment(sketch, "E357", {"start": v(-5.43, -2.7) * mm, "end": v(-5.32, -2.88) * mm});
            skLineSegment(sketch, "E358", {"start": v(-5.32, -2.88) * mm, "end": v(-5.21, -3.04) * mm});
            skLineSegment(sketch, "E359", {"start": v(-5.21, -3.04) * mm, "end": v(-5.1, -3.22) * mm});
            skLineSegment(sketch, "E360", {"start": v(-5.1, -3.22) * mm, "end": v(-5.25, -3.34) * mm});
            skLineSegment(sketch, "E361", {"start": v(-5.25, -3.34) * mm, "end": v(-5.4, -3.47) * mm});
            skLineSegment(sketch, "E362", {"start": v(-5.4, -3.47) * mm, "end": v(-5.54, -3.6) * mm});
            skLineSegment(sketch, "E363", {"start": v(-5.54, -3.6) * mm, "end": v(-5.7, -3.73) * mm});
            skLineSegment(sketch, "E364", {"start": v(-5.7, -3.73) * mm, "end": v(-5.84, -3.86) * mm});
            skLineSegment(sketch, "E365", {"start": v(-5.84, -3.86) * mm, "end": v(-5.99, -3.99) * mm});
            skLineSegment(sketch, "E366", {"start": v(-5.99, -3.99) * mm, "end": v(-6.14, -4.12) * mm});
            skLineSegment(sketch, "E367", {"start": v(-6.14, -4.12) * mm, "end": v(-6.29, -4.25) * mm});
            skLineSegment(sketch, "E368", {"start": v(-6.29, -4.25) * mm, "end": v(-6.43, -4.37) * mm});
            skLineSegment(sketch, "E369", {"start": v(-6.43, -4.37) * mm, "end": v(-6.58, -4.5) * mm});
            skLineSegment(sketch, "E370", {"start": v(-6.58, -4.5) * mm, "end": v(-6.7, -4.66) * mm});
            skLineSegment(sketch, "E371", {"start": v(-6.7, -4.66) * mm, "end": v(-6.8, -4.82) * mm});
            skLineSegment(sketch, "E372", {"start": v(-6.8, -4.82) * mm, "end": v(-6.9, -5) * mm});
            skLineSegment(sketch, "E373", {"start": v(-6.9, -5) * mm, "end": v(-6.97, -5.16) * mm});
            skLineSegment(sketch, "E374", {"start": v(-6.97, -5.16) * mm, "end": v(-7.04, -5.35) * mm});
            skLineSegment(sketch, "E375", {"start": v(-7.04, -5.35) * mm, "end": v(-7.1, -5.53) * mm});
            skLineSegment(sketch, "E376", {"start": v(-7.1, -5.53) * mm, "end": v(-7.14, -5.72) * mm});
            skLineSegment(sketch, "E377", {"start": v(-7.14, -5.72) * mm, "end": v(-7.17, -5.9) * mm});
            skLineSegment(sketch, "E378", {"start": v(-7.17, -5.9) * mm, "end": v(-7.19, -6.1) * mm});
            skLineSegment(sketch, "E379", {"start": v(-7.19, -6.1) * mm, "end": v(-7.2, -6.29) * mm});
            skLineSegment(sketch, "E380", {"start": v(-7.2, -6.29) * mm, "end": v(-7.18, -6.48) * mm});
            skLineSegment(sketch, "E381", {"start": v(-7.18, -6.48) * mm, "end": v(-7.17, -6.67) * mm});
            skLineSegment(sketch, "E382", {"start": v(-7.17, -6.67) * mm, "end": v(-6.97, -6.66) * mm});
            skLineSegment(sketch, "E383", {"start": v(-6.97, -6.66) * mm, "end": v(-6.78, -6.64) * mm});
            skLineSegment(sketch, "E384", {"start": v(-6.78, -6.64) * mm, "end": v(-6.59, -6.6) * mm});
            skLineSegment(sketch, "E385", {"start": v(-6.59, -6.6) * mm, "end": v(-6.4, -6.56) * mm});
            skLineSegment(sketch, "E386", {"start": v(-6.4, -6.56) * mm, "end": v(-6.22, -6.5) * mm});
            skLineSegment(sketch, "E387", {"start": v(-6.22, -6.5) * mm, "end": v(-6.04, -6.44) * mm});
            skLineSegment(sketch, "E388", {"start": v(-6.04, -6.44) * mm, "end": v(-5.87, -6.35) * mm});
            skLineSegment(sketch, "E389", {"start": v(-5.87, -6.35) * mm, "end": v(-5.7, -6.26) * mm});
            skLineSegment(sketch, "E390", {"start": v(-5.7, -6.26) * mm, "end": v(-5.54, -6.15) * mm});
            skLineSegment(sketch, "E391", {"start": v(-5.54, -6.15) * mm, "end": v(-5.39, -6.04) * mm});
            skLineSegment(sketch, "E392", {"start": v(-5.39, -6.04) * mm, "end": v(-5.24, -5.91) * mm});
            skLineSegment(sketch, "E393", {"start": v(-5.24, -5.91) * mm, "end": v(-5.1, -5.78) * mm});
            skLineSegment(sketch, "E394", {"start": v(-5.1, -5.78) * mm, "end": v(-5, -5.62) * mm});
            skLineSegment(sketch, "E395", {"start": v(-5, -5.62) * mm, "end": v(-4.9, -5.45) * mm});
            skLineSegment(sketch, "E396", {"start": v(-4.9, -5.45) * mm, "end": v(-4.79, -5.29) * mm});
            skLineSegment(sketch, "E397", {"start": v(-4.79, -5.29) * mm, "end": v(-4.68, -5.12) * mm});
            skLineSegment(sketch, "E398", {"start": v(-4.68, -5.12) * mm, "end": v(-4.57, -4.96) * mm});
            skLineSegment(sketch, "E399", {"start": v(-4.57, -4.96) * mm, "end": v(-4.47, -4.8) * mm});
            skLineSegment(sketch, "E400", {"start": v(-4.47, -4.8) * mm, "end": v(-4.36, -4.63) * mm});
            skLineSegment(sketch, "E401", {"start": v(-4.36, -4.63) * mm, "end": v(-4.25, -4.46) * mm});
            skLineSegment(sketch, "E402", {"start": v(-4.25, -4.46) * mm, "end": v(-4.15, -4.3) * mm});
            skLineSegment(sketch, "E403", {"start": v(-4.15, -4.3) * mm, "end": v(-4.04, -4.13) * mm});
            skLineSegment(sketch, "E404", {"start": v(-4.04, -4.13) * mm, "end": v(-3.86, -4.21) * mm});
            skLineSegment(sketch, "E405", {"start": v(-3.86, -4.21) * mm, "end": v(-3.68, -4.3) * mm});
            skLineSegment(sketch, "E406", {"start": v(-3.68, -4.3) * mm, "end": v(-3.5, -4.38) * mm});
            skLineSegment(sketch, "E407", {"start": v(-3.5, -4.38) * mm, "end": v(-3.32, -4.46) * mm});
            skLineSegment(sketch, "E408", {"start": v(-3.32, -4.46) * mm, "end": v(-3.14, -4.54) * mm});
            skLineSegment(sketch, "E409", {"start": v(-3.14, -4.54) * mm, "end": v(-2.96, -4.63) * mm});
            skLineSegment(sketch, "E410", {"start": v(-2.96, -4.63) * mm, "end": v(-2.77, -4.71) * mm});
            skLineSegment(sketch, "E411", {"start": v(-2.77, -4.71) * mm, "end": v(-2.83, -4.9) * mm});
            skLineSegment(sketch, "E412", {"start": v(-2.83, -4.9) * mm, "end": v(-2.88, -5.09) * mm});
            skLineSegment(sketch, "E413", {"start": v(-2.88, -5.09) * mm, "end": v(-2.94, -5.28) * mm});
            skLineSegment(sketch, "E414", {"start": v(-2.94, -5.28) * mm, "end": v(-3, -5.47) * mm});
            skLineSegment(sketch, "E415", {"start": v(-3, -5.47) * mm, "end": v(-3.05, -5.65) * mm});
            skLineSegment(sketch, "E416", {"start": v(-3.05, -5.65) * mm, "end": v(-3.1, -5.84) * mm});
            skLineSegment(sketch, "E417", {"start": v(-3.1, -5.84) * mm, "end": v(-3.16, -6.03) * mm});
            skLineSegment(sketch, "E418", {"start": v(-3.16, -6.03) * mm, "end": v(-3.21, -6.22) * mm});
            skLineSegment(sketch, "E419", {"start": v(-3.21, -6.22) * mm, "end": v(-3.27, -6.4) * mm});
            skLineSegment(sketch, "E420", {"start": v(-3.27, -6.4) * mm, "end": v(-3.32, -6.6) * mm});
            skLineSegment(sketch, "E421", {"start": v(-3.32, -6.6) * mm, "end": v(-3.33, -6.8) * mm});
            skLineSegment(sketch, "E422", {"start": v(-3.33, -6.8) * mm, "end": v(-3.33, -6.98) * mm});
            skLineSegment(sketch, "E423", {"start": v(-3.33, -6.98) * mm, "end": v(-3.32, -7.18) * mm});
            skLineSegment(sketch, "E424", {"start": v(-3.32, -7.18) * mm, "end": v(-3.3, -7.36) * mm});
            skLineSegment(sketch, "E425", {"start": v(-3.3, -7.36) * mm, "end": v(-3.25, -7.56) * mm});
            skLineSegment(sketch, "E426", {"start": v(-3.25, -7.56) * mm, "end": v(-3.2, -7.73) * mm});
            skLineSegment(sketch, "E427", {"start": v(-3.2, -7.73) * mm, "end": v(-3.13, -7.92) * mm});
            skLineSegment(sketch, "E428", {"start": v(-3.13, -7.92) * mm, "end": v(-3.06, -8.1) * mm});
            skLineSegment(sketch, "E429", {"start": v(-3.06, -8.1) * mm, "end": v(-2.97, -8.27) * mm});
            skLineSegment(sketch, "E430", {"start": v(-2.97, -8.27) * mm, "end": v(-2.87, -8.43) * mm});
            skLineSegment(sketch, "E431", {"start": v(-2.87, -8.43) * mm, "end": v(-2.76, -8.59) * mm});
            skLineSegment(sketch, "E432", {"start": v(-2.76, -8.59) * mm, "end": v(-2.64, -8.73) * mm});
            skLineSegment(sketch, "E433", {"start": v(-2.64, -8.73) * mm, "end": v(-2.48, -8.62) * mm});
            skLineSegment(sketch, "E434", {"start": v(-2.48, -8.62) * mm, "end": v(-2.34, -8.5) * mm});
            skLineSegment(sketch, "E435", {"start": v(-2.34, -8.5) * mm, "end": v(-2.19, -8.37) * mm});
            skLineSegment(sketch, "E436", {"start": v(-2.19, -8.37) * mm, "end": v(-2.06, -8.24) * mm});
            skLineSegment(sketch, "E437", {"start": v(-2.06, -8.24) * mm, "end": v(-1.94, -8.08) * mm});
            skLineSegment(sketch, "E438", {"start": v(-1.94, -8.08) * mm, "end": v(-1.83, -7.93) * mm});
            skLineSegment(sketch, "E439", {"start": v(-1.83, -7.93) * mm, "end": v(-1.72, -7.76) * mm});
            skLineSegment(sketch, "E440", {"start": v(-1.72, -7.76) * mm, "end": v(-1.63, -7.6) * mm});
            skLineSegment(sketch, "E441", {"start": v(-1.63, -7.6) * mm, "end": v(-1.55, -7.42) * mm});
            skLineSegment(sketch, "E442", {"start": v(-1.55, -7.42) * mm, "end": v(-1.49, -7.25) * mm});
            skLineSegment(sketch, "E443", {"start": v(-1.49, -7.25) * mm, "end": v(-1.43, -7.06) * mm});
            skLineSegment(sketch, "E444", {"start": v(-1.43, -7.06) * mm, "end": v(-1.39, -6.88) * mm});
            skLineSegment(sketch, "E445", {"start": v(-1.39, -6.88) * mm, "end": v(-1.39, -6.68) * mm});
            skLineSegment(sketch, "E446", {"start": v(-1.39, -6.68) * mm, "end": v(-1.39, -6.48) * mm});
            skLineSegment(sketch, "E447", {"start": v(-1.39, -6.48) * mm, "end": v(-1.39, -6.29) * mm});
            skLineSegment(sketch, "E448", {"start": v(-1.39, -6.29) * mm, "end": v(-1.39, -6.09) * mm});
            skLineSegment(sketch, "E449", {"start": v(-1.39, -6.09) * mm, "end": v(-1.39, -5.9) * mm});
            skLineSegment(sketch, "E450", {"start": v(-1.39, -5.9) * mm, "end": v(-1.39, -5.7) * mm});
            skLineSegment(sketch, "E451", {"start": v(-1.39, -5.7) * mm, "end": v(-1.39, -5.5) * mm});
            skLineSegment(sketch, "E452", {"start": v(-1.39, -5.5) * mm, "end": v(-1.39, -5.3) * mm});
            skLineSegment(sketch, "E453", {"start": v(-1.39, -5.3) * mm, "end": v(-1.39, -5.1) * mm});
            skLineSegment(sketch, "E454", {"start": v(-1.39, -5.1) * mm, "end": v(-1.39, -4.91) * mm});
            skLineSegment(sketch, "E455", {"start": v(-1.39, -4.91) * mm, "end": v(-1.2, -4.88) * mm});
            skLineSegment(sketch, "E456", {"start": v(-1.2, -4.88) * mm, "end": v(-1, -4.85) * mm});
            skLineSegment(sketch, "E457", {"start": v(-1, -4.85) * mm, "end": v(-0.8, -4.83) * mm});
            skLineSegment(sketch, "E458", {"start": v(-0.8, -4.83) * mm, "end": v(-0.6, -4.8) * mm});
            skLineSegment(sketch, "E459", {"start": v(-0.6, -4.8) * mm, "end": v(-0.4, -4.77) * mm});
            skLineSegment(sketch, "E460", {"start": v(-0.4, -4.77) * mm, "end": v(-0.2, -4.74) * mm});
            skLineSegment(sketch, "E461", {"start": v(-0.2, -4.74) * mm, "end": v(0, -4.71) * mm});
            skLineSegment(sketch, "E462", {"start": v(0, -4.71) * mm, "end": v(0.05, -4.9) * mm});
            skLineSegment(sketch, "E463", {"start": v(0.05, -4.9) * mm, "end": v(0.1, -5.09) * mm});
            skLineSegment(sketch, "E464", {"start": v(0.1, -5.09) * mm, "end": v(0.16, -5.28) * mm});
            skLineSegment(sketch, "E465", {"start": v(0.16, -5.28) * mm, "end": v(0.22, -5.47) * mm});
            skLineSegment(sketch, "E466", {"start": v(0.22, -5.47) * mm, "end": v(0.27, -5.65) * mm});
            skLineSegment(sketch, "E467", {"start": v(0.27, -5.65) * mm, "end": v(0.33, -5.84) * mm});
            skLineSegment(sketch, "E468", {"start": v(0.33, -5.84) * mm, "end": v(0.38, -6.03) * mm});
            skLineSegment(sketch, "E469", {"start": v(0.38, -6.03) * mm, "end": v(0.44, -6.22) * mm});
            skLineSegment(sketch, "E470", {"start": v(0.44, -6.22) * mm, "end": v(0.5, -6.4) * mm});
            skLineSegment(sketch, "E471", {"start": v(0.5, -6.4) * mm, "end": v(0.55, -6.6) * mm});
            skLineSegment(sketch, "E472", {"start": v(0.55, -6.6) * mm, "end": v(0.65, -6.77) * mm});
            skLineSegment(sketch, "E473", {"start": v(0.65, -6.77) * mm, "end": v(0.75, -6.92) * mm});
            skLineSegment(sketch, "E474", {"start": v(0.75, -6.92) * mm, "end": v(0.87, -7.08) * mm});
            skLineSegment(sketch, "E475", {"start": v(0.87, -7.08) * mm, "end": v(1, -7.22) * mm});
            skLineSegment(sketch, "E476", {"start": v(1, -7.22) * mm, "end": v(1.13, -7.36) * mm});
            skLineSegment(sketch, "E477", {"start": v(1.13, -7.36) * mm, "end": v(1.27, -7.49) * mm});
            skLineSegment(sketch, "E478", {"start": v(1.27, -7.49) * mm, "end": v(1.43, -7.6) * mm});
            skLineSegment(sketch, "E479", {"start": v(1.43, -7.6) * mm, "end": v(1.58, -7.71) * mm});
            skLineSegment(sketch, "E480", {"start": v(1.58, -7.71) * mm, "end": v(1.75, -7.8) * mm});
            skLineSegment(sketch, "E481", {"start": v(1.75, -7.8) * mm, "end": v(1.92, -7.9) * mm});
            skLineSegment(sketch, "E482", {"start": v(1.92, -7.9) * mm, "end": v(2.1, -7.97) * mm});
            skLineSegment(sketch, "E483", {"start": v(2.1, -7.97) * mm, "end": v(2.28, -8.03) * mm});
            skLineSegment(sketch, "E484", {"start": v(2.28, -8.03) * mm, "end": v(2.35, -7.84) * mm});
            skLineSegment(sketch, "E485", {"start": v(2.35, -7.84) * mm, "end": v(2.41, -7.67) * mm});
            skLineSegment(sketch, "E486", {"start": v(2.41, -7.67) * mm, "end": v(2.46, -7.47) * mm});
            skLineSegment(sketch, "E487", {"start": v(2.46, -7.47) * mm, "end": v(2.5, -7.3) * mm});
            skLineSegment(sketch, "E488", {"start": v(2.5, -7.3) * mm, "end": v(2.52, -7.1) * mm});
            skLineSegment(sketch, "E489", {"start": v(2.52, -7.1) * mm, "end": v(2.53, -6.91) * mm});
            skLineSegment(sketch, "E490", {"start": v(2.53, -6.91) * mm, "end": v(2.53, -6.71) * mm});
            skLineSegment(sketch, "E491", {"start": v(2.53, -6.71) * mm, "end": v(2.52, -6.53) * mm});
            skLineSegment(sketch, "E492", {"start": v(2.52, -6.53) * mm, "end": v(2.49, -6.33) * mm});
            skLineSegment(sketch, "E493", {"start": v(2.49, -6.33) * mm, "end": v(2.45, -6.15) * mm});
            skLineSegment(sketch, "E494", {"start": v(2.45, -6.15) * mm, "end": v(2.4, -5.96) * mm});
            skLineSegment(sketch, "E495", {"start": v(2.4, -5.96) * mm, "end": v(2.33, -5.78) * mm});
            skLineSegment(sketch, "E496", {"start": v(2.33, -5.78) * mm, "end": v(2.22, -5.62) * mm});
            skLineSegment(sketch, "E497", {"start": v(2.22, -5.62) * mm, "end": v(2.12, -5.45) * mm});
            skLineSegment(sketch, "E498", {"start": v(2.12, -5.45) * mm, "end": v(2.01, -5.29) * mm});
            skLineSegment(sketch, "E499", {"start": v(2.01, -5.29) * mm, "end": v(1.9, -5.12) * mm});
            skLineSegment(sketch, "E500", {"start": v(1.9, -5.12) * mm, "end": v(1.8, -4.96) * mm});
            skLineSegment(sketch, "E501", {"start": v(1.8, -4.96) * mm, "end": v(1.7, -4.8) * mm});
            skLineSegment(sketch, "E502", {"start": v(1.7, -4.8) * mm, "end": v(1.59, -4.63) * mm});
            skLineSegment(sketch, "E503", {"start": v(1.59, -4.63) * mm, "end": v(1.48, -4.46) * mm});
            skLineSegment(sketch, "E504", {"start": v(1.48, -4.46) * mm, "end": v(1.37, -4.3) * mm});
            skLineSegment(sketch, "E505", {"start": v(1.37, -4.3) * mm, "end": v(1.27, -4.13) * mm});
            skLineSegment(sketch, "E506", {"start": v(1.27, -4.13) * mm, "end": v(1.42, -4) * mm});
            skLineSegment(sketch, "E507", {"start": v(1.42, -4) * mm, "end": v(1.57, -3.87) * mm});
            skLineSegment(sketch, "E508", {"start": v(1.57, -3.87) * mm, "end": v(1.72, -3.74) * mm});
            skLineSegment(sketch, "E509", {"start": v(1.72, -3.74) * mm, "end": v(1.87, -3.61) * mm});
            skLineSegment(sketch, "E510", {"start": v(1.87, -3.61) * mm, "end": v(2.02, -3.48) * mm});
            skLineSegment(sketch, "E511", {"start": v(2.02, -3.48) * mm, "end": v(2.17, -3.35) * mm});
            skLineSegment(sketch, "E512", {"start": v(2.17, -3.35) * mm, "end": v(2.32, -3.22) * mm});
            skLineSegment(sketch, "E513", {"start": v(2.32, -3.22) * mm, "end": v(2.47, -3.34) * mm});
            skLineSegment(sketch, "E514", {"start": v(2.47, -3.34) * mm, "end": v(2.62, -3.47) * mm});
            skLineSegment(sketch, "E515", {"start": v(2.62, -3.47) * mm, "end": v(2.77, -3.6) * mm});
            skLineSegment(sketch, "E516", {"start": v(2.77, -3.6) * mm, "end": v(2.92, -3.73) * mm});
            skLineSegment(sketch, "E517", {"start": v(2.92, -3.73) * mm, "end": v(3.07, -3.86) * mm});
            skLineSegment(sketch, "E518", {"start": v(3.07, -3.86) * mm, "end": v(3.22, -3.99) * mm});
            skLineSegment(sketch, "E519", {"start": v(3.22, -3.99) * mm, "end": v(3.36, -4.12) * mm});
            skLineSegment(sketch, "E520", {"start": v(3.36, -4.12) * mm, "end": v(3.51, -4.25) * mm});
            skLineSegment(sketch, "E521", {"start": v(3.51, -4.25) * mm, "end": v(3.66, -4.37) * mm});
            skLineSegment(sketch, "E522", {"start": v(3.66, -4.37) * mm, "end": v(3.8, -4.5) * mm});
            skLineSegment(sketch, "E523", {"start": v(3.8, -4.5) * mm, "end": v(3.98, -4.6) * mm});
            skLineSegment(sketch, "E524", {"start": v(3.98, -4.6) * mm, "end": v(4.15, -4.67) * mm});
            skLineSegment(sketch, "E525", {"start": v(4.15, -4.67) * mm, "end": v(4.34, -4.74) * mm});
            skLineSegment(sketch, "E526", {"start": v(4.34, -4.74) * mm, "end": v(4.52, -4.8) * mm});
            skLineSegment(sketch, "E527", {"start": v(4.52, -4.8) * mm, "end": v(4.71, -4.83) * mm});
            skLineSegment(sketch, "E528", {"start": v(4.71, -4.83) * mm, "end": v(4.9, -4.86) * mm});
            skLineSegment(sketch, "E529", {"start": v(4.9, -4.86) * mm, "end": v(5.1, -4.88) * mm});
            skLineSegment(sketch, "E530", {"start": v(5.1, -4.88) * mm, "end": v(5.28, -4.88) * mm});
            skLineSegment(sketch, "E531", {"start": v(5.28, -4.88) * mm, "end": v(5.48, -4.87) * mm});
            skLineSegment(sketch, "E532", {"start": v(5.48, -4.87) * mm, "end": v(5.66, -4.85) * mm});
            skLineSegment(sketch, "E533", {"start": v(5.66, -4.85) * mm, "end": v(5.86, -4.82) * mm});
            skLineSegment(sketch, "E534", {"start": v(5.86, -4.82) * mm, "end": v(6.04, -4.77) * mm});
            skLineSegment(sketch, "E535", {"start": v(6.04, -4.77) * mm, "end": v(6, -4.58) * mm});
            skLineSegment(sketch, "E536", {"start": v(6, -4.58) * mm, "end": v(5.95, -4.4) * mm});
            skLineSegment(sketch, "E537", {"start": v(5.95, -4.4) * mm, "end": v(5.9, -4.2) * mm});
            skLineSegment(sketch, "E538", {"start": v(5.9, -4.2) * mm, "end": v(5.82, -4.03) * mm});
            skLineSegment(sketch, "E539", {"start": v(5.82, -4.03) * mm, "end": v(5.74, -3.86) * mm});
            skLineSegment(sketch, "E540", {"start": v(5.74, -3.86) * mm, "end": v(5.65, -3.7) * mm});
            skLineSegment(sketch, "E541", {"start": v(5.65, -3.7) * mm, "end": v(5.54, -3.53) * mm});
            skLineSegment(sketch, "E542", {"start": v(5.54, -3.53) * mm, "end": v(5.42, -3.38) * mm});
            skLineSegment(sketch, "E543", {"start": v(5.42, -3.38) * mm, "end": v(5.3, -3.23) * mm});
            skLineSegment(sketch, "E544", {"start": v(5.3, -3.23) * mm, "end": v(5.16, -3.1) * mm});
            skLineSegment(sketch, "E545", {"start": v(5.16, -3.1) * mm, "end": v(5.01, -2.97) * mm});
            skLineSegment(sketch, "E546", {"start": v(5.01, -2.97) * mm, "end": v(4.87, -2.86) * mm});
            skLineSegment(sketch, "E547", {"start": v(4.87, -2.86) * mm, "end": v(4.69, -2.77) * mm});
            skLineSegment(sketch, "E548", {"start": v(4.69, -2.77) * mm, "end": v(4.5, -2.7) * mm});
            skLineSegment(sketch, "E549", {"start": v(4.5, -2.7) * mm, "end": v(4.33, -2.61) * mm});
            skLineSegment(sketch, "E550", {"start": v(4.33, -2.61) * mm, "end": v(4.15, -2.53) * mm});
            skLineSegment(sketch, "E551", {"start": v(4.15, -2.53) * mm, "end": v(3.97, -2.45) * mm});
            skLineSegment(sketch, "E552", {"start": v(3.97, -2.45) * mm, "end": v(3.8, -2.37) * mm});
            skLineSegment(sketch, "E553", {"start": v(3.8, -2.37) * mm, "end": v(3.62, -2.29) * mm});
            skLineSegment(sketch, "E554", {"start": v(3.62, -2.29) * mm, "end": v(3.44, -2.2) * mm});
            skLineSegment(sketch, "E555", {"start": v(3.44, -2.2) * mm, "end": v(3.26, -2.12) * mm});
            skLineSegment(sketch, "E556", {"start": v(3.26, -2.12) * mm, "end": v(3.08, -2.04) * mm});
            skLineSegment(sketch, "E557", {"start": v(3.08, -2.04) * mm, "end": v(3.14, -1.85) * mm});
            skLineSegment(sketch, "E558", {"start": v(3.14, -1.85) * mm, "end": v(3.2, -1.66) * mm});
            skLineSegment(sketch, "E559", {"start": v(3.2, -1.66) * mm, "end": v(3.25, -1.47) * mm});
            skLineSegment(sketch, "E560", {"start": v(3.25, -1.47) * mm, "end": v(3.3, -1.28) * mm});
            skLineSegment(sketch, "E561", {"start": v(3.3, -1.28) * mm, "end": v(3.36, -1.09) * mm});
            skLineSegment(sketch, "E562", {"start": v(3.36, -1.09) * mm, "end": v(3.42, -0.9) * mm});
            skLineSegment(sketch, "E563", {"start": v(3.42, -0.9) * mm, "end": v(3.47, -0.7) * mm});
            skCircle(sketch, "E564", {"center": v(-1.39, 0) * mm, "radius": 1 * mm});
            skSolve(sketch);
        }
        {
            var Q0;
            Q0=makeQuery(id+"F0.imprint","IMPRINT",FACE,{"disambiguationData":[TD([[makeQuery(id+"F0.imprint","IMPRINT",EDGE,{"derivedFrom":sQuery(id+"F0.wireOp",EDGE,"E0")}),1.0]])]});
            extrude(context, id + "F1", {"entities" : qUnion([Q0]), "depth" : 7 * mm});
        }
    });
